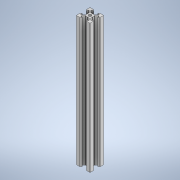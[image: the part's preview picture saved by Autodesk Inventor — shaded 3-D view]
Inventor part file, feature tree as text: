
AUTODESK INVENTOR PART (.ipt)
format: ipt  version: 2021 (Build 250183000, 183)  size: 237,056 bytes
history: native  units: mm
features: sketch x4, extrude x2, fillet x2, other x1, pattern_circular x1, hole x1, projected_geometry x1
ambient origin geometry x8: Origin, YZ Plane, XZ Plane, XY Plane, X Axis, Y Axis, Z Axis, Center Point
bodies: Body1 (feature_tree)
feature tree (12):
  other  "實體1"
  extrude  "擠出1"  Depth=20.0mm
  extrude  "擠出2"  Depth=20.0mm
  fillet  "圓角1"  Radius=190.0mm
  pattern_circular  "環形陣列1"  [2 undecoded]
  hole  "孔1"  [1 undecoded]
  fillet  "圓角2"  Radius=6.2mm
  sketch  "草圖4"
  sketch  "草圖1"
  sketch  "草圖2"
  projected_geometry  "投影迴路1"
  sketch  "草圖3"
note: 3 required parameter values undecoded (feature->parameter linkage not recoverable at this tier; creation-order binding heuristic only, values carry confidence <= 0.55)
